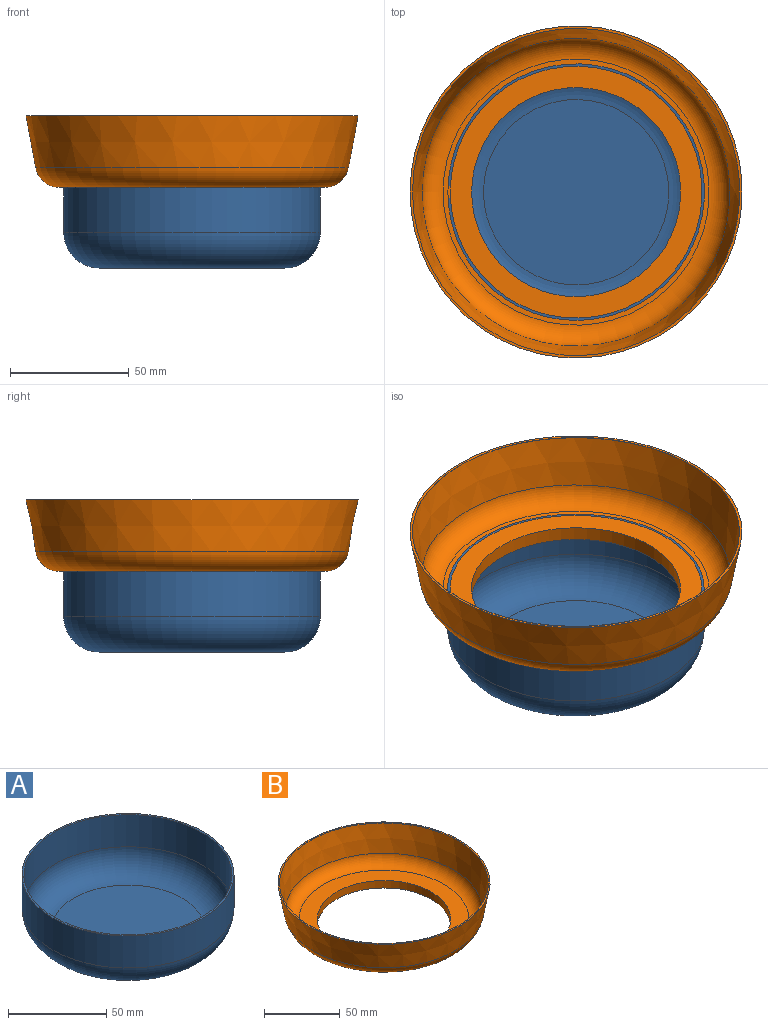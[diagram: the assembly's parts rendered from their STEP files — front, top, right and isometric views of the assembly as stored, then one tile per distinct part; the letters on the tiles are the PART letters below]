
ASSEMBLY  parts=2 mates=1
PART A: 7 faces, bbox 116.9x116.9x35 mm
  f0: cylinder r=54mm len=108mm, axis (0,0,-1), area 6785.8mm2, adj f1,f6
  f1: torus R=39mm, axis (0,0,-1), area 7187.4mm2, adj f0,f2
  f2: plane 78x78mm, normal (0,0,-1), area 4778.4mm2, adj f1
  f3: plane 78x78mm, normal (0,0,1), area 4778.4mm2, adj f4
  f4: torus R=39mm, axis (0,0,-1), area 6620.3mm2, adj f3,f5
  f5: cylinder r=53mm len=106mm, axis (0,0,-1), area 6660.2mm2, adj f4,f6
  f6: plane 108x108mm, normal (0,0,1), area 336.2mm2, adj f0,f5
PART B: 11 faces, bbox 142.9x142.9x35 mm
  f0: cylinder r=68.87mm len=137.73mm, axis (0,0,-1), area 47.8mm2, adj f1,f10
  f1: plane 139.81x139.81mm, normal (0,0,1), area 452.5mm2, adj f0,f2
  f2: cone r=69.9mm half-angle=10.6deg, axis (0,0,1), area 9471mm2, adj f1,f3
  f3: torus R=56mm, axis (0,0,-1), area 5391.2mm2, adj f2,f4
  f4: plane 112x112mm, normal (0,0,-1), area 2613.8mm2, adj f3,f5
  f5: cone r=48mm half-angle=11.3deg, axis (0,0,1), area 1521.8mm2, adj f4,f6
  f6: plane 94x94mm, normal (0,0,-1), area 857.7mm2, adj f5,f7
  f7: cylinder r=44mm len=88mm, axis (0,0,-1), area 1658.8mm2, adj f6,f8
  f8: plane 112x112mm, normal (0,0,1), area 3769.9mm2, adj f7,f9
  f9: torus R=56mm, axis (0,0,-1), area 4805.9mm2, adj f8,f10
  f10: cone r=64.85mm half-angle=10.6deg, axis (0,0,1), area 9204.4mm2, adj f0,f9
PLACE A t=(-2.28,2.03,-47.47)mm
PLACE B t=(-2.28,2.03,-13.47)mm
MATE fastened B.f5 <-> A.f0  axis (0,0,1) through (-2.28,2.03,-12.47)mm
